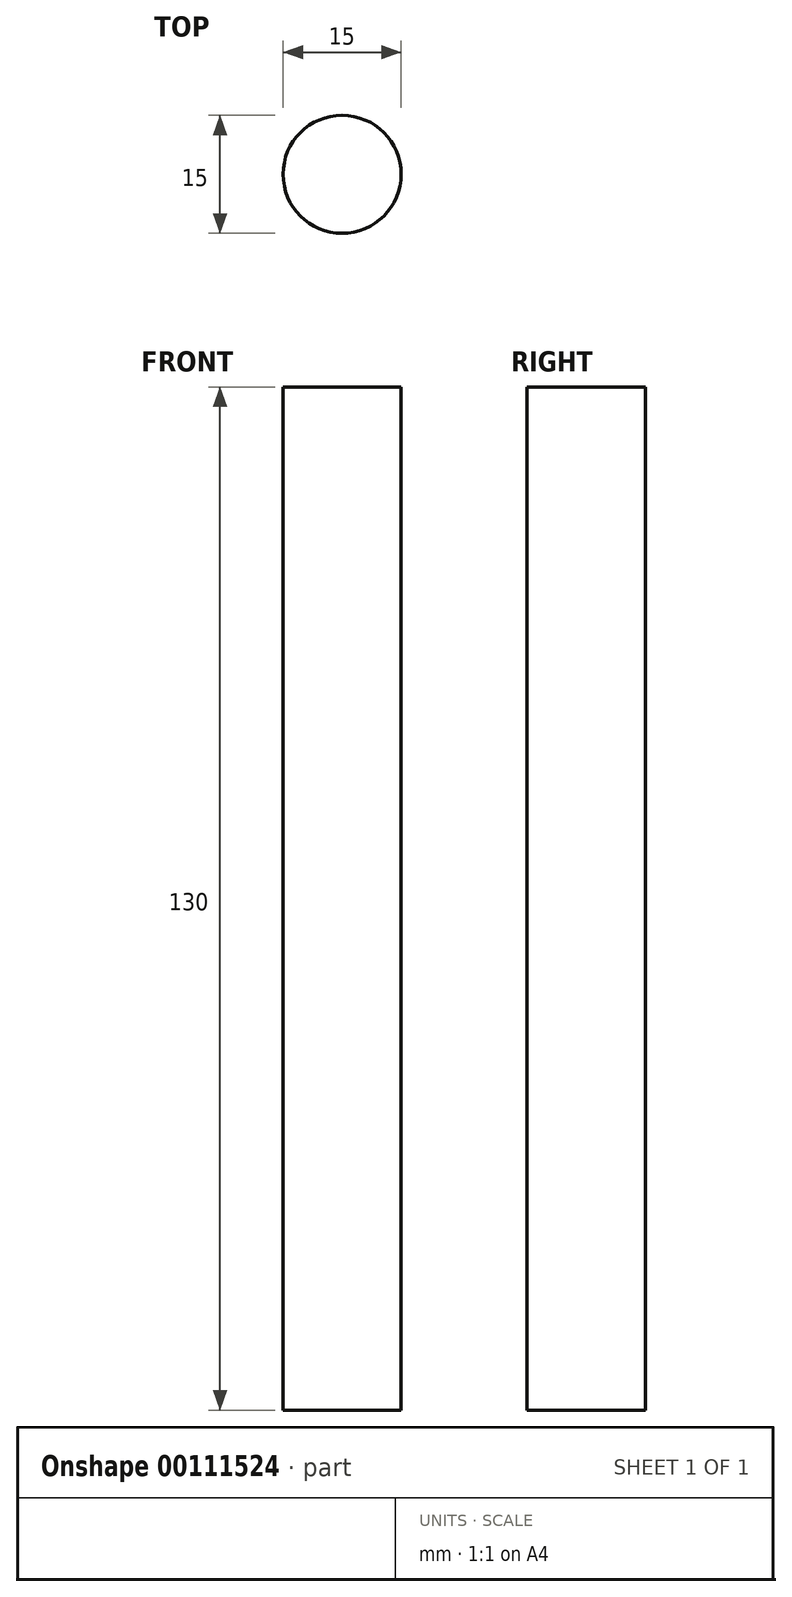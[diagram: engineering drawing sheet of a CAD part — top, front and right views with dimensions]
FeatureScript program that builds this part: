
annotation { "Feature Type Name" : "Feature", "Feature Type Description" : "" }
export const myFeature = defineFeature(function(context is Context, id is Id, definition is map)
    precondition{}
    {
        {
            var Q0;
            Q0=qCreatedBy(makeId("Top.planeOp"),FACE);
            var sketch = newSketch(context, id + "F0", { "sketchPlane" : qUnion([Q0])});
            skCircle(sketch, "E0", {"center": v(0, 0) * mm, "radius": 7.5 * mm});
            skSolve(sketch);
        }
        {
            var Q0;
            Q0=makeQuery(id+"F0.imprint","IMPRINT",FACE,{"disambiguationData":[TD([[makeQuery(id+"F0.imprint","IMPRINT",EDGE,{"derivedFrom":sQuery(id+"F0.wireOp",EDGE,"E0")}),1.0]])]});
            extrude(context, id + "F1", {"entities" : qUnion([Q0]), "depth" : 130 * mm});
        }
    });
